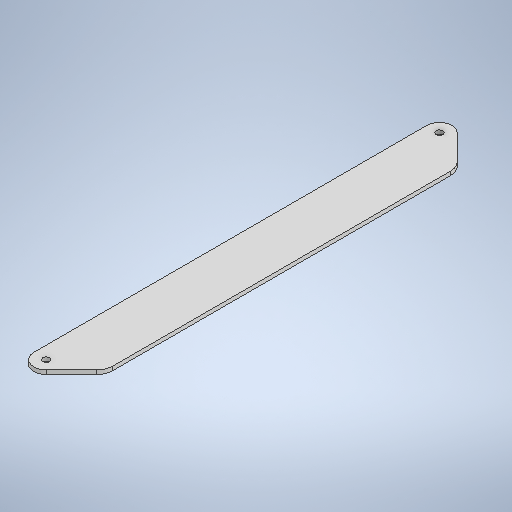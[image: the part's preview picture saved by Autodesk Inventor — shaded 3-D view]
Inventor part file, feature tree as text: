
AUTODESK INVENTOR PART (.ipt)
format: ipt  version: 2025.2 (Build 292293000, 293)  size: 272,896 bytes
history: native  units: in
note: dims shown in document units (in); Inventor stores cm internally (conversion verified against a paired STEP export)
features: extrude x2, sketch x2
ambient origin geometry x8: Origin, YZ Plane, XZ Plane, XY Plane, X Axis, Y Axis, Z Axis, Center Point
bodies: Solid1 (feature_tree)
feature tree (4):
  extrude  "Extrusion1"  Depth=6.6929in
  extrude  "Extrusion2"  Depth=0.0669in
  sketch  "Sketch1"  dims[d0=0.4291in d3=6.6929in]
  sketch  "Sketch2"  dims[d5=0.0in d6=0.4724in d7=0.4724in d8=0.2146in d9=45.0deg d10=0.2756in d11=0.2756in d12=0.4291in d13=135.0deg d14=0.0669in d15=0.0in d16=0.1181in d17=0.1181in d18=0.0669in d19=0.0in]
